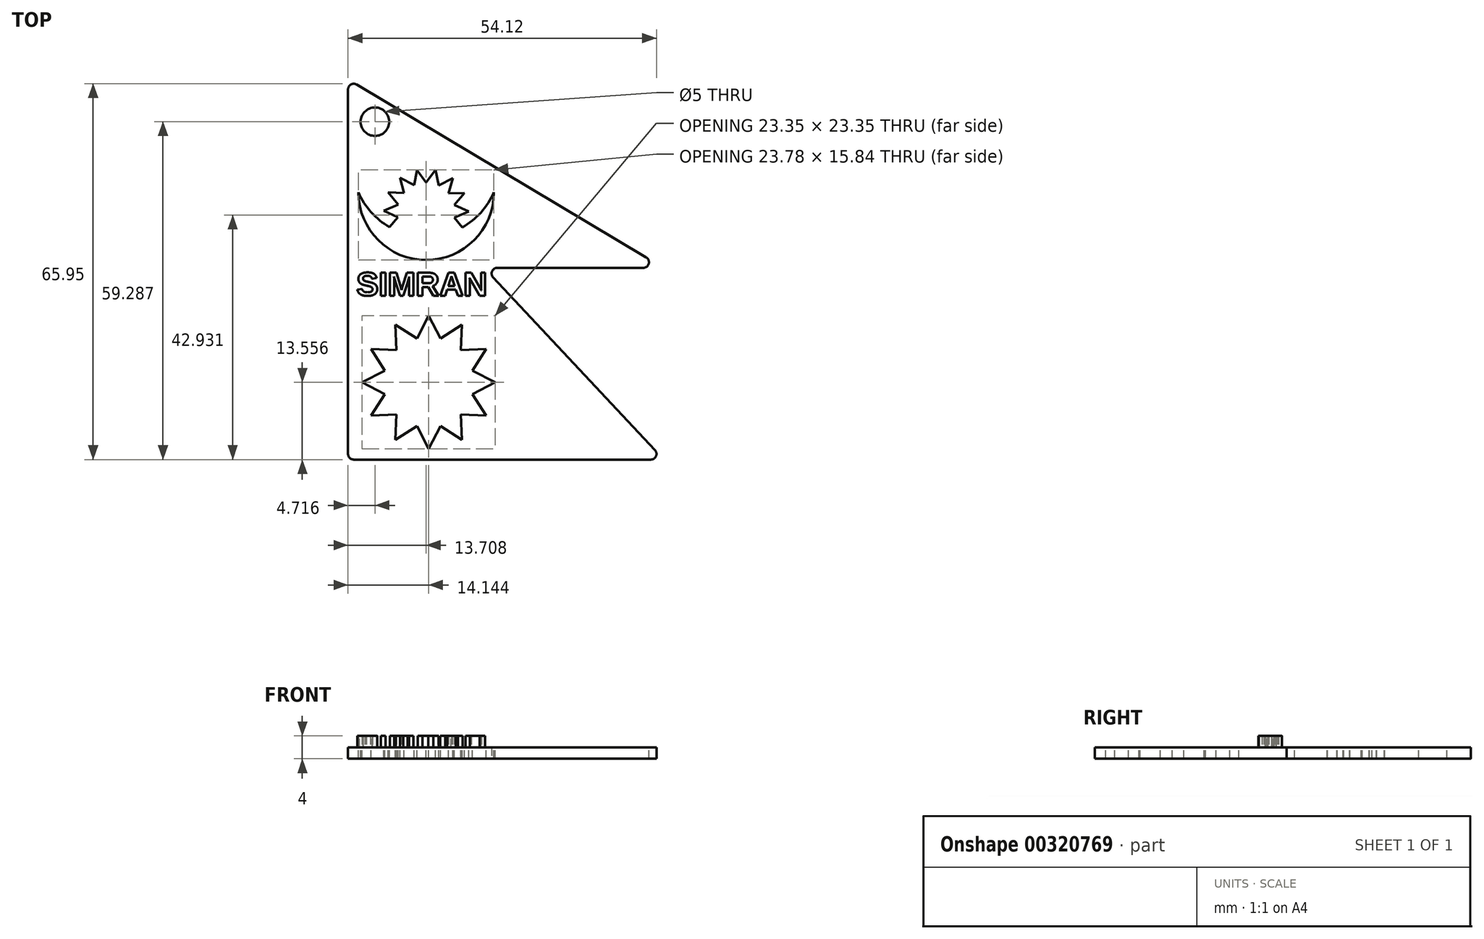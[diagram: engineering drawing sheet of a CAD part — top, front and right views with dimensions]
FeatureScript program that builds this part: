
annotation { "Feature Type Name" : "Feature", "Feature Type Description" : "" }
export const myFeature = defineFeature(function(context is Context, id is Id, definition is map)
    precondition{}
    {
        {
            var Q0;
            Q0=qCreatedBy(makeId("Top.planeOp"),FACE);
            var sketch = newSketch(context, id + "F0", { "sketchPlane" : qUnion([Q0])});
            skLineSegment(sketch, "E0", {"start": v(0, 66.7) * mm, "end": v(0, 0) * mm});
            skLineSegment(sketch, "E1", {"start": v(0, 66.7) * mm, "end": v(55.43, 33.64) * mm});
            skLineSegment(sketch, "E2", {"start": v(55.43, 33.64) * mm, "end": v(23.9, 33.64) * mm});
            skLineSegment(sketch, "E3", {"start": v(23.9, 33.64) * mm, "end": v(55.43, 0) * mm});
            skLineSegment(sketch, "E4", {"start": v(55.43, 0) * mm, "end": v(0, 0) * mm});
            skLineSegment(sketch, "E5", {"start": v(14.14, 25.23) * mm, "end": v(12.08, 21.25) * mm});
            skLineSegment(sketch, "E6.MirrorCS", {"start": v(14.14, 25.23) * mm, "end": v(16.2, 21.25) * mm});
            skLineSegment(sketch, "E7.1.0", {"start": v(19.98, 23.67) * mm, "end": v(19.78, 19.19) * mm});
            skLineSegment(sketch, "E7.1.1", {"start": v(19.98, 23.67) * mm, "end": v(16.2, 21.25) * mm});
            skLineSegment(sketch, "E7.2.0", {"start": v(24.25, 19.4) * mm, "end": v(21.84, 15.62) * mm});
            skLineSegment(sketch, "E7.2.1", {"start": v(24.25, 19.4) * mm, "end": v(19.78, 19.19) * mm});
            skLineSegment(sketch, "E7.3.0", {"start": v(25.82, 13.56) * mm, "end": v(21.84, 11.5) * mm});
            skLineSegment(sketch, "E7.3.1", {"start": v(25.82, 13.56) * mm, "end": v(21.84, 15.62) * mm});
            skLineSegment(sketch, "E7.4.0", {"start": v(24.25, 7.72) * mm, "end": v(19.78, 7.92) * mm});
            skLineSegment(sketch, "E7.4.1", {"start": v(24.25, 7.72) * mm, "end": v(21.84, 11.5) * mm});
            skLineSegment(sketch, "E7.5.0", {"start": v(19.98, 3.45) * mm, "end": v(16.2, 5.86) * mm});
            skLineSegment(sketch, "E7.5.1", {"start": v(19.98, 3.45) * mm, "end": v(19.78, 7.92) * mm});
            skLineSegment(sketch, "E7.6.0", {"start": v(14.14, 1.88) * mm, "end": v(12.08, 5.86) * mm});
            skLineSegment(sketch, "E7.6.1", {"start": v(14.14, 1.88) * mm, "end": v(16.2, 5.86) * mm});
            skLineSegment(sketch, "E7.7.0", {"start": v(8.3, 3.45) * mm, "end": v(8.51, 7.92) * mm});
            skLineSegment(sketch, "E7.7.1", {"start": v(8.3, 3.45) * mm, "end": v(12.08, 5.86) * mm});
            skLineSegment(sketch, "E7.8.0", {"start": v(4.03, 7.72) * mm, "end": v(6.45, 11.5) * mm});
            skLineSegment(sketch, "E7.8.1", {"start": v(4.03, 7.72) * mm, "end": v(8.51, 7.92) * mm});
            skLineSegment(sketch, "E7.9.0", {"start": v(2.47, 13.56) * mm, "end": v(6.45, 15.62) * mm});
            skLineSegment(sketch, "E7.9.1", {"start": v(2.47, 13.56) * mm, "end": v(6.45, 11.5) * mm});
            skLineSegment(sketch, "E7.10.0", {"start": v(4.03, 19.4) * mm, "end": v(8.51, 19.19) * mm});
            skLineSegment(sketch, "E7.10.1", {"start": v(4.03, 19.4) * mm, "end": v(6.45, 15.62) * mm});
            skLineSegment(sketch, "E7.11.0", {"start": v(8.3, 23.67) * mm, "end": v(12.08, 21.25) * mm});
            skLineSegment(sketch, "E7.11.1", {"start": v(8.3, 23.67) * mm, "end": v(8.51, 19.19) * mm});
            skSolve(sketch);
        }
        {
            var Q0;
            Q0=makeQuery(id+"F0.imprint","IMPRINT",FACE,{"disambiguationData":[TD([[makeQuery(id+"F0.imprint","IMPRINT",EDGE,{"derivedFrom":sQuery(id+"F0.wireOp",EDGE,"E0")}),1.0]])]});
            var sketch = newSketch(context, id + "F1", { "sketchPlane" : qUnion([Q0])});
            skArc(sketch, "E8", {"start": v(1.82, 46.9) * mm, "mid": v(13.7, 35.01) * mm, "end": v(25.6, 46.9) * mm});
            skArc(sketch, "E9", {"start": v(1.82, 46.9) * mm, "mid": v(4.06, 43.4) * mm, "end": v(7.29, 40.79) * mm});
            skLineSegment(sketch, "E10", {"start": v(13.7, 48.63) * mm, "end": v(12.12, 50.75) * mm});
            skLineSegment(sketch, "E11.MirrorCS", {"start": v(13.7, 48.63) * mm, "end": v(15.37, 50.85) * mm});
            skLineSegment(sketch, "E12.1.0", {"start": v(15.9, 48.13) * mm, "end": v(15.37, 50.85) * mm});
            skLineSegment(sketch, "E12.1.1", {"start": v(15.9, 48.13) * mm, "end": v(18.37, 49.4) * mm});
            skLineSegment(sketch, "E12.2.0", {"start": v(17.66, 46.72) * mm, "end": v(18.37, 49.4) * mm});
            skLineSegment(sketch, "E12.2.1", {"start": v(17.66, 46.72) * mm, "end": v(20.43, 46.8) * mm});
            skLineSegment(sketch, "E12.3.0", {"start": v(18.64, 44.7) * mm, "end": v(20.43, 46.8) * mm});
            skLineSegment(sketch, "E12.3.1", {"start": v(18.64, 44.7) * mm, "end": v(21.17, 43.56) * mm});
            skLineSegment(sketch, "E12.4.0", {"start": v(18.63, 42.44) * mm, "end": v(21.17, 43.56) * mm});
            skLineSegment(sketch, "E12.4.1", {"start": v(18.63, 42.44) * mm, "end": v(20.05, 40.75) * mm});
            skLineSegment(sketch, "E12.10.0", {"start": v(8.77, 42.5) * mm, "end": v(7.29, 40.79) * mm});
            skLineSegment(sketch, "E12.10.1", {"start": v(8.77, 42.5) * mm, "end": v(6.25, 43.66) * mm});
            skLineSegment(sketch, "E12.11.0", {"start": v(8.8, 44.76) * mm, "end": v(6.25, 43.66) * mm});
            skLineSegment(sketch, "E12.11.1", {"start": v(8.8, 44.76) * mm, "end": v(7.02, 46.9) * mm});
            skLineSegment(sketch, "E12.12.0", {"start": v(9.8, 46.78) * mm, "end": v(7.02, 46.9) * mm});
            skLineSegment(sketch, "E12.12.1", {"start": v(9.8, 46.78) * mm, "end": v(9.13, 49.47) * mm});
            skLineSegment(sketch, "E12.13.0", {"start": v(11.57, 48.16) * mm, "end": v(9.13, 49.47) * mm});
            skLineSegment(sketch, "E12.13.1", {"start": v(11.57, 48.16) * mm, "end": v(12.12, 50.75) * mm});
            skArc(sketch, "E13.trimOffspring", {"start": v(20.05, 40.75) * mm, "mid": v(23.33, 43.37) * mm, "end": v(25.6, 46.9) * mm});
            skSolve(sketch);
        }
        {
            var Q0;
            Q0=makeQuery(id+"F0.imprint","IMPRINT",FACE,{"disambiguationData":[TD([[makeQuery(id+"F0.imprint","IMPRINT",EDGE,{"derivedFrom":sQuery(id+"F0.wireOp",EDGE,"E0")}),1.0]])]});
            extrude(context, id + "F2", {"entities" : qUnion([Q0]), "oppositeDirection" : true, "depth" : 2 * mm});
        }
        {
            var Q0;
            Q0=makeQuery(id+"F1.imprint","IMPRINT",FACE,{"disambiguationData":[TD([[makeQuery(id+"F1.imprint","IMPRINT",EDGE,{"derivedFrom":sQuery(id+"F1.wireOp",EDGE,"E8")}),1.0]])]});
            extrude(context, id + "F3", {"entities" : qUnion([Q0]), "operationType" : NewBodyOperationType.REMOVE, "oppositeDirection" : true, "depth" : 25 * mm});
        }
        {
            var Q0;
            Q0=makeQuery(id+"F2.opExtrude","SWEPT_EDGE",EDGE,{"disambiguationData":[OSD([sQuery(id+"F0.wireOp",EDGE,"E0"),sQuery(id+"F0.wireOp",EDGE,"E4")])]});
            var Q1;
            Q1=makeQuery(id+"F2.opExtrude","SWEPT_EDGE",EDGE,{"disambiguationData":[OSD([sQuery(id+"F0.wireOp",EDGE,"E3"),sQuery(id+"F0.wireOp",EDGE,"E4")])]});
            var Q2;
            Q2=makeQuery(id+"F2.opExtrude","SWEPT_EDGE",EDGE,{"disambiguationData":[OSD([sQuery(id+"F0.wireOp",EDGE,"E2"),sQuery(id+"F0.wireOp",EDGE,"E3")])]});
            var Q3;
            Q3=makeQuery(id+"F2.opExtrude","SWEPT_EDGE",EDGE,{"disambiguationData":[OSD([sQuery(id+"F0.wireOp",EDGE,"E1"),sQuery(id+"F0.wireOp",EDGE,"E2")])]});
            var Q4;
            Q4=makeQuery(id+"F2.opExtrude","SWEPT_EDGE",EDGE,{"disambiguationData":[OSD([sQuery(id+"F0.wireOp",EDGE,"E0"),sQuery(id+"F0.wireOp",EDGE,"E1")])]});
            fillet(context, id + "F4", {"entities" : qUnion([Q0, Q1, Q2, Q3, Q4]), "radius" : 1 * mm, "tangentPropagation" : true, "allowEdgeOverflow" : false});
        }
        {
            var Q0;
            Q0=makeQuery(id+"F2.opExtrude","CAP_FACE",FACE,{"disambiguationData":[OSD([sQuery(id+"F0.wireOp",EDGE,"E0"),sQuery(id+"F0.wireOp",EDGE,"E1"),sQuery(id+"F0.wireOp",EDGE,"E2"),sQuery(id+"F0.wireOp",EDGE,"E3"),sQuery(id+"F0.wireOp",EDGE,"E4"),sQuery(id+"F0.wireOp",EDGE,"E5"),sQuery(id+"F0.wireOp",EDGE,"E6.MirrorCS"),sQuery(id+"F0.wireOp",EDGE,"E7.1.0"),sQuery(id+"F0.wireOp",EDGE,"E7.1.1"),sQuery(id+"F0.wireOp",EDGE,"E7.2.0"),sQuery(id+"F0.wireOp",EDGE,"E7.2.1"),sQuery(id+"F0.wireOp",EDGE,"E7.3.0"),sQuery(id+"F0.wireOp",EDGE,"E7.3.1"),sQuery(id+"F0.wireOp",EDGE,"E7.4.0"),sQuery(id+"F0.wireOp",EDGE,"E7.4.1"),sQuery(id+"F0.wireOp",EDGE,"E7.5.0"),sQuery(id+"F0.wireOp",EDGE,"E7.5.1"),sQuery(id+"F0.wireOp",EDGE,"E7.6.0"),sQuery(id+"F0.wireOp",EDGE,"E7.6.1"),sQuery(id+"F0.wireOp",EDGE,"E7.7.0"),sQuery(id+"F0.wireOp",EDGE,"E7.7.1"),sQuery(id+"F0.wireOp",EDGE,"E7.8.0"),sQuery(id+"F0.wireOp",EDGE,"E7.8.1"),sQuery(id+"F0.wireOp",EDGE,"E7.9.0"),sQuery(id+"F0.wireOp",EDGE,"E7.9.1"),sQuery(id+"F0.wireOp",EDGE,"E7.10.0"),sQuery(id+"F0.wireOp",EDGE,"E7.10.1"),sQuery(id+"F0.wireOp",EDGE,"E7.11.0"),sQuery(id+"F0.wireOp",EDGE,"E7.11.1")])],"isStart":true});
            var sketch = newSketch(context, id + "F5", { "sketchPlane" : qUnion([Q0])});
            skText(sketch, "E14", { "text": "SIMRAN", "fontName": "Arimo-Bold.ttf"});
            skPoint(sketch, "E14.firstSnap0", {"position": v(0, 32.97) * mm});
            const initialGuessF5  = {"E14": [0.00146, 0.02877, 1, 0, 0.0042]};
            skSetInitialGuess(sketch, initialGuessF5);
            skSolve(sketch);
        }
        {
            var Q0;
            Q0=qSketchRegion(id+"F5",true);
            extrude(context, id + "F6", {"entities" : qUnion([Q0]), "operationType" : NewBodyOperationType.ADD, "depth" : 2 * mm});
        }
        {
            var Q0;
            {var subQ0=sQuery(id+"F0.wireOp",EDGE,"E4");var subQ1=sQuery(id+"F0.wireOp",EDGE,"E3");var subQ2=sQuery(id+"F0.wireOp",EDGE,"E7.7.1");var subQ3=sQuery(id+"F0.wireOp",EDGE,"E0");var subQ4=sQuery(id+"F0.wireOp",EDGE,"E7.10.1");var subQ5=sQuery(id+"F0.wireOp",EDGE,"E2");var subQ6=sQuery(id+"F0.wireOp",EDGE,"E7.11.1");var subQ7=sQuery(id+"F0.wireOp",EDGE,"E7.7.0");var subQ8=sQuery(id+"F0.wireOp",EDGE,"E1");var subQ9=sQuery(id+"F0.wireOp",EDGE,"E7.10.0");var subQ10=sQuery(id+"F0.wireOp",EDGE,"E7.3.0");var subQ11=sQuery(id+"F0.wireOp",EDGE,"E7.6.0");var subQ12=sQuery(id+"F0.wireOp",EDGE,"E7.2.1");var subQ13=sQuery(id+"F0.wireOp",EDGE,"E7.5.1");var subQ14=sQuery(id+"F0.wireOp",EDGE,"E7.3.1");var subQ15=sQuery(id+"F0.wireOp",EDGE,"E7.6.1");var subQ16=sQuery(id+"F0.wireOp",EDGE,"E7.11.0");var subQ17=sQuery(id+"F0.wireOp",EDGE,"E7.8.0");var subQ18=sQuery(id+"F0.wireOp",EDGE,"E7.2.0");var subQ19=sQuery(id+"F0.wireOp",EDGE,"E7.9.1");var subQ20=sQuery(id+"F0.wireOp",EDGE,"E7.4.0");var subQ21=sQuery(id+"F0.wireOp",EDGE,"E5");var subQ22=sQuery(id+"F0.wireOp",EDGE,"E7.4.1");var subQ23=sQuery(id+"F0.wireOp",EDGE,"E6.MirrorCS");var subQ24=sQuery(id+"F0.wireOp",EDGE,"E7.5.0");var subQ25=sQuery(id+"F0.wireOp",EDGE,"E7.1.0");var subQ26=sQuery(id+"F0.wireOp",EDGE,"E7.8.1");var subQ27=sQuery(id+"F0.wireOp",EDGE,"E7.1.1");var subQ28=sQuery(id+"F0.wireOp",EDGE,"E7.9.0");Q0=makeQuery(id+"F6.boolean.opBoolean","SPLIT",FACE,{"disambiguationData":[TD([makeQuery(id+"F2.opExtrude","SWEPT_FACE",FACE,{"disambiguationData":[OSD([subQ3])]})])],"derivedFrom":makeQuery(id+"F2.opExtrude","CAP_FACE",FACE,{"disambiguationData":[OSD([subQ3,subQ8,subQ5,subQ1,subQ0,subQ21,subQ23,subQ25,subQ27,subQ18,subQ12,subQ10,subQ14,subQ20,subQ22,subQ24,subQ13,subQ11,subQ15,subQ7,subQ2,subQ17,subQ26,subQ28,subQ19,subQ9,subQ4,subQ16,subQ6])],"isStart":true})});}
            var sketch = newSketch(context, id + "F7", { "sketchPlane" : qUnion([Q0])});
            skCircle(sketch, "E15", {"center": v(4.72, 59.29) * mm, "radius": 2.5 * mm});
            skSolve(sketch);
        }
        {
            var Q0;
            Q0=makeQuery(id+"F7.imprint","IMPRINT",FACE,{"disambiguationData":[TD([[makeQuery(id+"F7.imprint","IMPRINT",EDGE,{"derivedFrom":sQuery(id+"F7.wireOp",EDGE,"E15")}),1.0]])]});
            extrude(context, id + "F8", {"entities" : qUnion([Q0]), "operationType" : NewBodyOperationType.REMOVE, "oppositeDirection" : true, "depth" : 25 * mm});
        }
    });
